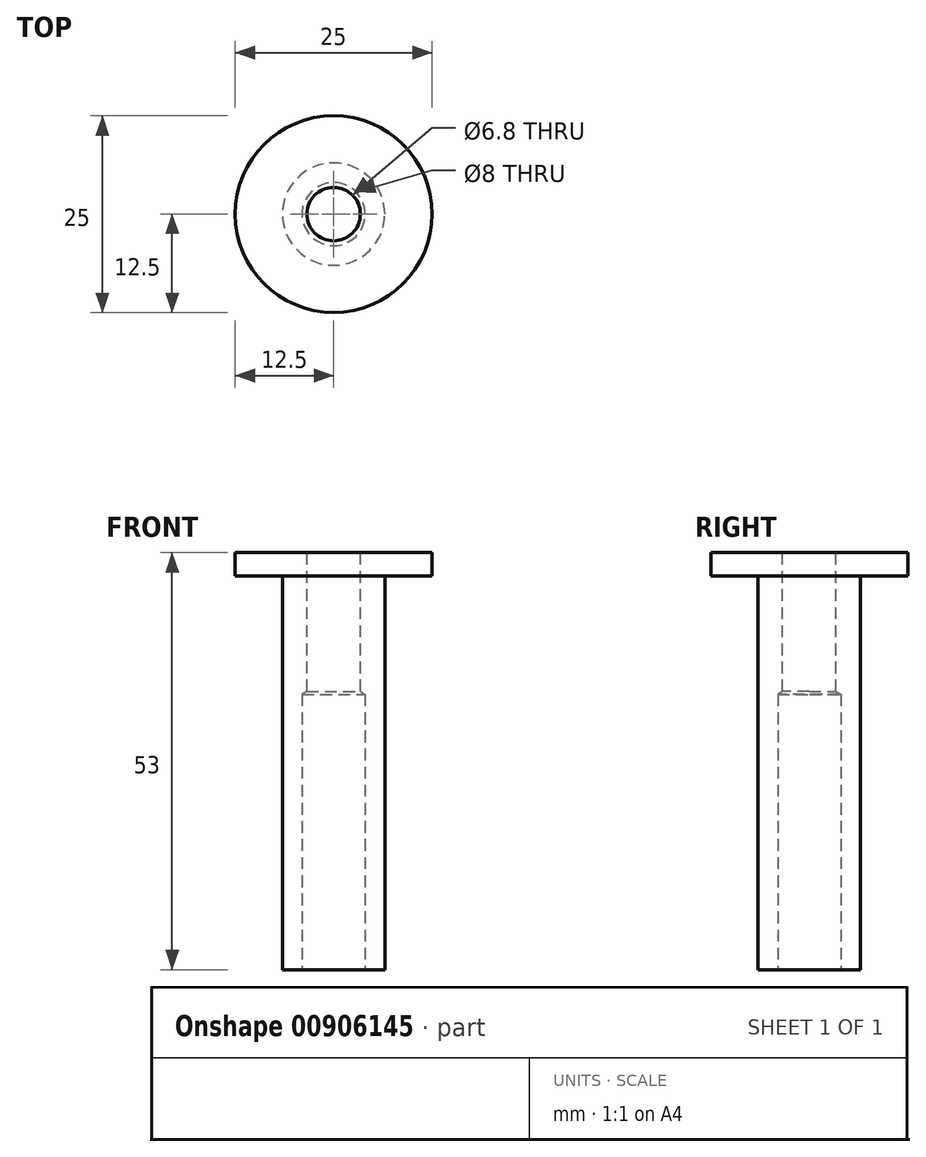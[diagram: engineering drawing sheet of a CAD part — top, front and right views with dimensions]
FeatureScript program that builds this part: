
annotation { "Feature Type Name" : "Feature", "Feature Type Description" : "" }
export const myFeature = defineFeature(function(context is Context, id is Id, definition is map)
    precondition{}
    {
        {
            var Q0;
            Q0=qCreatedBy(makeId("Front.planeOp"),FACE);
            var sketch = newSketch(context, id + "F0", { "sketchPlane" : qUnion([Q0])});
            skLineSegment(sketch, "E0", {"start": v(0, 0) * mm, "end": v(0, 53) * mm});
            skLineSegment(sketch, "E1", {"start": v(0, 53) * mm, "end": v(12.5, 53) * mm});
            skLineSegment(sketch, "E2", {"start": v(12.5, 53) * mm, "end": v(12.5, 50) * mm});
            skLineSegment(sketch, "E3", {"start": v(12.5, 50) * mm, "end": v(6.5, 50) * mm});
            skLineSegment(sketch, "E4", {"start": v(6.5, 50) * mm, "end": v(6.5, 0) * mm});
            skLineSegment(sketch, "E5", {"start": v(6.5, 0) * mm, "end": v(0, 0) * mm});
            skLineSegment(sketch, "E6", {"start": v(0, 0) * mm, "end": v(0, 71.61) * mm, "construction": true});
            skSolve(sketch);
        }
        {
            var Q0;
            Q0 = qSketchRegion(id + "F0", true);
            var Q1;
            Q1=sQuery(id+"F0.wireOp",EDGE,"E6");
            revolve(context, id + "F1", {"surfaceOperationType" : NewSurfaceOperationType.NEW, "entities" : qUnion([Q0]), "axis" : qUnion([Q1]), "revolveType" : RevolveType.FULL});
        }
        {
            var Q0;
            Q0=makeQuery(id+"F1.opRevolve","SWEPT_FACE",FACE,{"disambiguationData":[OSD([sQuery(id+"F0.wireOp",EDGE,"E1")])]});
            var sketch = newSketch(context, id + "F2", { "sketchPlane" : qUnion([Q0])});
            skPoint(sketch, "E7", {"position": v(0, 0) * mm});
            skSolve(sketch);
        }
        {
            var Q0;
            Q0=sQuery(id+"F2.wireOp",VERTEX,"E7");
            var Q1;
            Q1=makeQuery(id+"F1.opRevolve","SWEPT_BODY",BODY,{"disambiguationData":[OSD([sQuery(id+"F0.wireOp",EDGE,"E0"),sQuery(id+"F0.wireOp",EDGE,"E1"),sQuery(id+"F0.wireOp",EDGE,"E2"),sQuery(id+"F0.wireOp",EDGE,"E3"),sQuery(id+"F0.wireOp",EDGE,"E4"),sQuery(id+"F0.wireOp",EDGE,"E5")])]});
            hole(context, id + "F3", {"style" : HoleStyle.SIMPLE, "endStyle" : HoleEndStyle.BLIND, "standardTappedOrClearance" : lookupTablePath({ "standard" : "ISO", "engagement" : "75%", "pitch" : "1.25 mm", "size" : "M8", "type" : "Tapped" }), "standardBlindInLast" : lookupTablePath({ "standard" : "ISO", "engagement" : "75%", "pitch" : "1.25 mm", "size" : "M8", "type" : "Tapped" }), "holeDiameter" : 6.8 * mm, "majorDiameter" : 8 * mm, "showTappedDepth" : true, "holeDepth" : 20 * mm, "isTappedThrough" : true, "tappedDepth" : 20 * mm, "tapClearance" : 0, "locations" : qUnion([Q0]), "scope" : qUnion([Q1])});
        }
        {
            var Q0;
            Q0=makeQuery(id+"F1.opRevolve","SWEPT_FACE",FACE,{"disambiguationData":[OSD([sQuery(id+"F0.wireOp",EDGE,"E5")])]});
            var sketch = newSketch(context, id + "F4", { "sketchPlane" : qUnion([Q0])});
            skPoint(sketch, "E8", {"position": v(0, 0) * mm});
            skSolve(sketch);
        }
        {
            var Q0;
            Q0=sQuery(id+"F4.wireOp",VERTEX,"E8");
            var Q1;
            Q1=makeQuery(id+"F1.opRevolve","SWEPT_BODY",BODY,{"disambiguationData":[OSD([sQuery(id+"F0.wireOp",EDGE,"E0"),sQuery(id+"F0.wireOp",EDGE,"E1"),sQuery(id+"F0.wireOp",EDGE,"E2"),sQuery(id+"F0.wireOp",EDGE,"E3"),sQuery(id+"F0.wireOp",EDGE,"E4"),sQuery(id+"F0.wireOp",EDGE,"E5")])]});
            hole(context, id + "F5", {"style" : HoleStyle.SIMPLE, "endStyle" : HoleEndStyle.BLIND, "holeDiameter" : 8 * mm, "majorDiameter" : 8 * mm, "holeDepth" : 35 * mm, "isTappedThrough" : true, "tappedDepth" : 16.25 * mm, "tapClearance" : 3, "locations" : qUnion([Q0]), "scope" : qUnion([Q1])});
        }
    });
